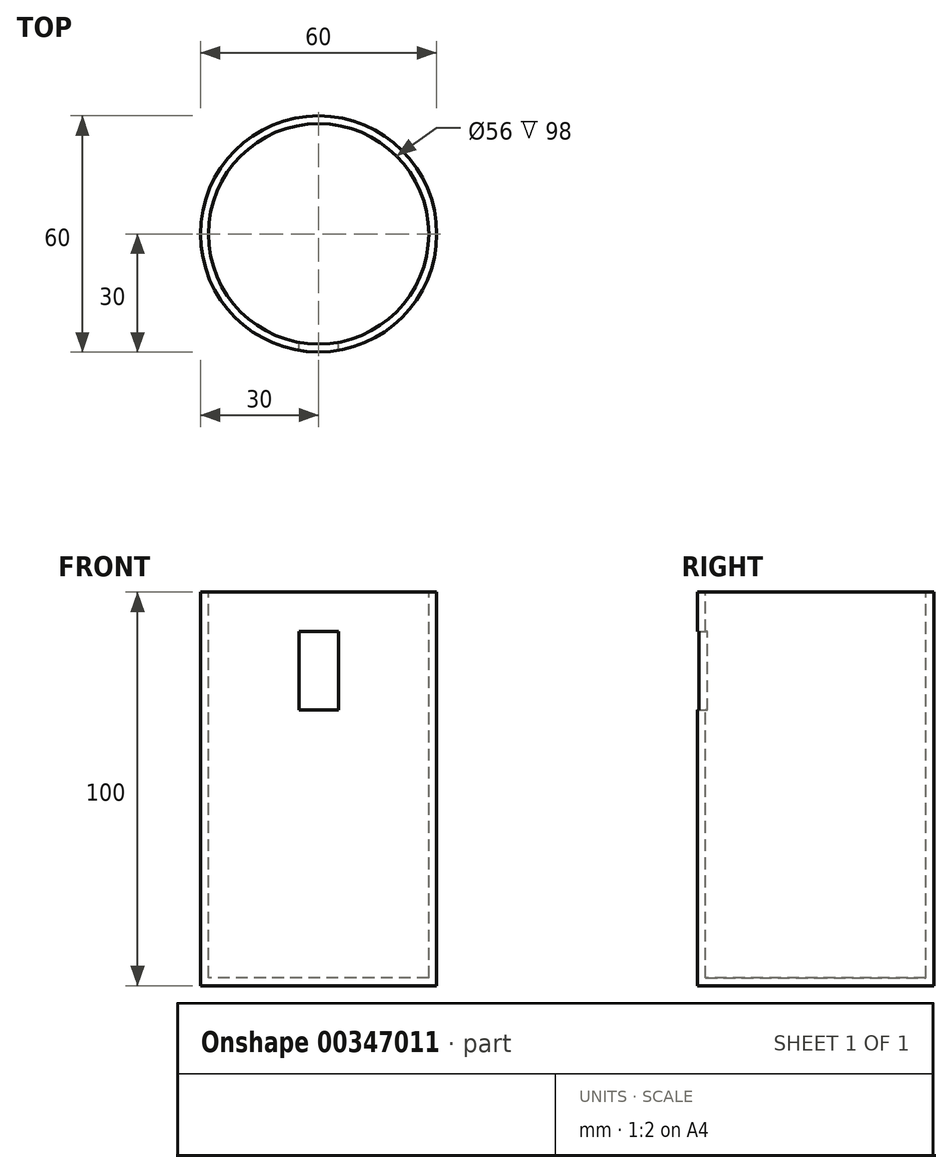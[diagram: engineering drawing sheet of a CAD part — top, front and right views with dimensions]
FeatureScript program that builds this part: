
annotation { "Feature Type Name" : "Feature", "Feature Type Description" : "" }
export const myFeature = defineFeature(function(context is Context, id is Id, definition is map)
    precondition{}
    {
        {
            var Q0;
            Q0=qCreatedBy(makeId("Top.planeOp"),FACE);
            var sketch = newSketch(context, id + "F0", { "sketchPlane" : qUnion([Q0])});
            skCircle(sketch, "E0", {"center": v(0, 0) * mm, "radius": 30 * mm});
            skSolve(sketch);
        }
        {
            var Q0;
            Q0=makeQuery(id+"F0.imprint","IMPRINT",FACE,{"disambiguationData":[TD([[makeQuery(id+"F0.imprint","IMPRINT",EDGE,{"derivedFrom":sQuery(id+"F0.wireOp",EDGE,"E0")}),1.0]])]});
            extrude(context, id + "F1", {"entities" : qUnion([Q0]), "depth" : 100 * mm});
        }
        {
            var Q0;
            Q0=makeQuery(id+"F1.opExtrude","CAP_FACE",FACE,{"disambiguationData":[OSD([sQuery(id+"F0.wireOp",EDGE,"E0")])],"isStart":false});
            var sketch = newSketch(context, id + "F2", { "sketchPlane" : qUnion([Q0])});
            skCircle(sketch, "E1", {"center": v(0, 0) * mm, "radius": 28 * mm});
            skSolve(sketch);
        }
        {
            var Q0;
            Q0=makeQuery(id+"F2.imprint","IMPRINT",FACE,{"disambiguationData":[TD([[makeQuery(id+"F2.imprint","IMPRINT",EDGE,{"derivedFrom":sQuery(id+"F2.wireOp",EDGE,"E1")}),1.0]])]});
            extrude(context, id + "F3", {"entities" : qUnion([Q0]), "operationType" : NewBodyOperationType.REMOVE, "oppositeDirection" : true, "depth" : 98 * mm});
        }
        {
            var Q0;
            Q0=qCreatedBy(makeId("Front.planeOp"),FACE);
            var sketch = newSketch(context, id + "F4", { "sketchPlane" : qUnion([Q0])});
            skLineSegment(sketch, "E2.bottom", {"start": v(-5, 90) * mm, "end": v(5, 90) * mm});
            skLineSegment(sketch, "E2.top", {"start": v(-5, 70) * mm, "end": v(5, 70) * mm});
            skLineSegment(sketch, "E2.left", {"start": v(-5, 90) * mm, "end": v(-5, 70) * mm});
            skLineSegment(sketch, "E2.right", {"start": v(5, 90) * mm, "end": v(5, 70) * mm});
            skSolve(sketch);
        }
        {
            var Q0;
            Q0=makeQuery(id+"F4.imprint","IMPRINT",FACE,{"disambiguationData":[TD([[makeQuery(id+"F4.imprint","IMPRINT",EDGE,{"derivedFrom":sQuery(id+"F4.wireOp",EDGE,"E2.bottom")}),-1.0]])]});
            extrude(context, id + "F5", {"entities" : qUnion([Q0]), "operationType" : NewBodyOperationType.REMOVE, "depth" : 30 * mm});
        }
    });
